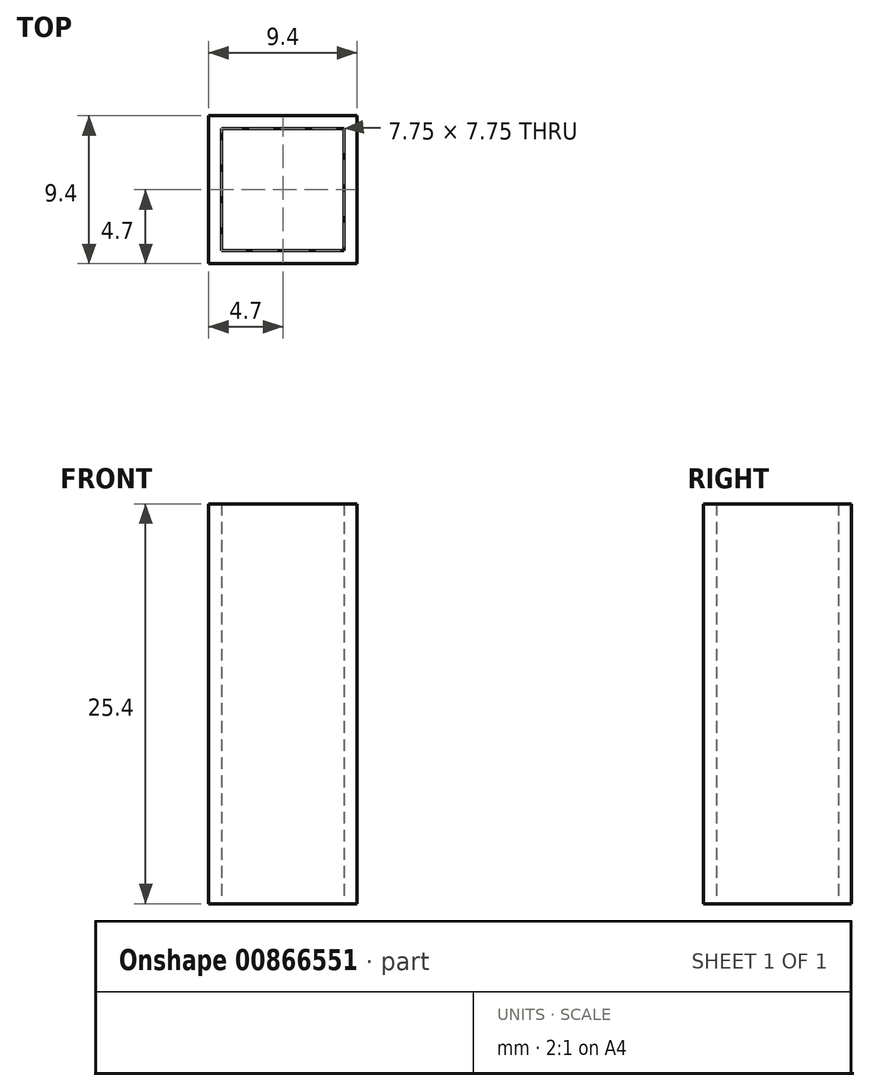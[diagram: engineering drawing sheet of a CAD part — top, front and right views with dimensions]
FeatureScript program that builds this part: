
annotation { "Feature Type Name" : "Feature", "Feature Type Description" : "" }
export const myFeature = defineFeature(function(context is Context, id is Id, definition is map)
    precondition{}
    {
        {
            var Q0;
            Q0=qCreatedBy(makeId("Top.planeOp"),FACE);
            var sketch = newSketch(context, id + "F0", { "sketchPlane" : qUnion([Q0])});
            skLineSegment(sketch, "E0.bottom", {"start": v(4.7, -4.7) * mm, "end": v(-4.7, -4.7) * mm});
            skLineSegment(sketch, "E0.top", {"start": v(4.7, 4.7) * mm, "end": v(-4.7, 4.7) * mm});
            skLineSegment(sketch, "E0.left", {"start": v(4.7, -4.7) * mm, "end": v(4.7, 4.7) * mm});
            skLineSegment(sketch, "E0.right", {"start": v(-4.7, -4.7) * mm, "end": v(-4.7, 4.7) * mm});
            skPoint(sketch, "E0.middle", {"position": v(0, 0) * mm});
            skLineSegment(sketch, "E1.bottom", {"start": v(3.87, -3.87) * mm, "end": v(-3.87, -3.87) * mm});
            skLineSegment(sketch, "E1.top", {"start": v(3.87, 3.87) * mm, "end": v(-3.87, 3.87) * mm});
            skLineSegment(sketch, "E1.left", {"start": v(3.87, -3.87) * mm, "end": v(3.87, 3.87) * mm});
            skLineSegment(sketch, "E1.right", {"start": v(-3.87, -3.87) * mm, "end": v(-3.87, 3.87) * mm});
            skSolve(sketch);
        }
        {
            var Q0;
            Q0=makeQuery(id+"F0.imprint","IMPRINT",FACE,{"disambiguationData":[TD([[makeQuery(id+"F0.imprint","IMPRINT",EDGE,{"derivedFrom":sQuery(id+"F0.wireOp",EDGE,"E0.bottom")}),-1.0]])]});
            extrude(context, id + "F1", {"entities" : qUnion([Q0]), "depth" : 25.4 * mm, "offsetDistance" : 25.4 * mm});
        }
    });
